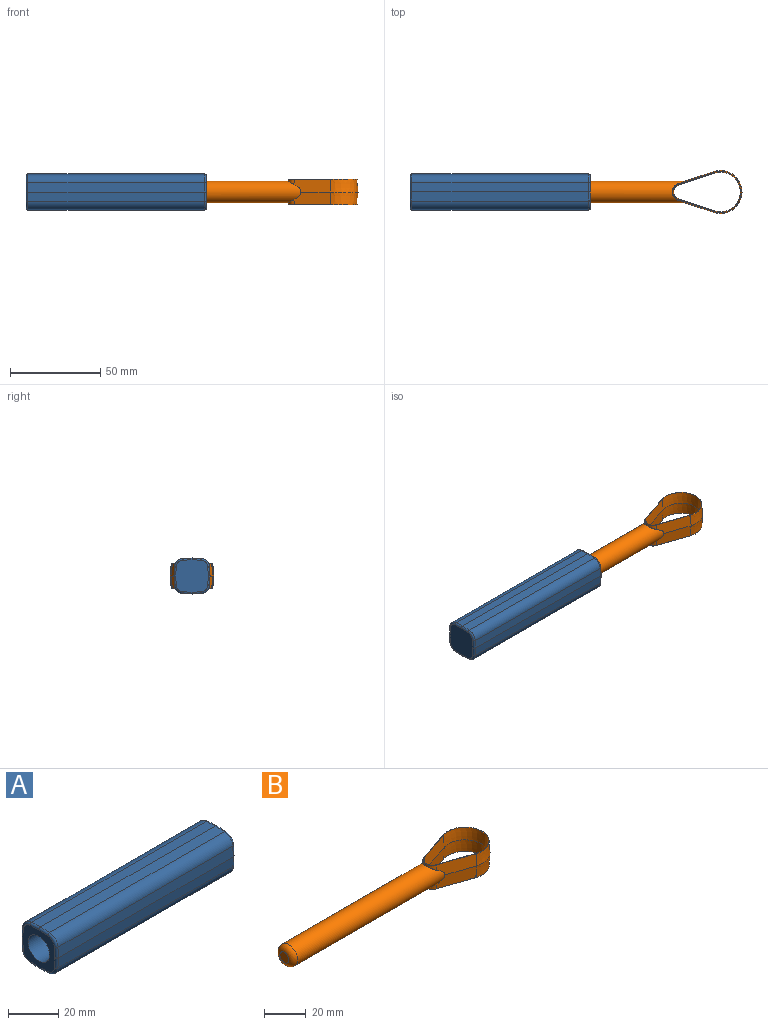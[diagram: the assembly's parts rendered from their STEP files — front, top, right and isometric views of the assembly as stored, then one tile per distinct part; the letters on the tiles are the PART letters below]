
ASSEMBLY  parts=2 mates=1
PART A: 40 faces, bbox 100x20.3x20.3 mm
  f0: plane 98x5.01mm, normal (0,1,0.05), area 491.3mm2, adj f1,f11,f22,f34
  f1: cylinder r=5mm len=98mm, axis (-1,0,0), area 718.4mm2, adj f0,f2,f20,f32
  f2: plane 98x5.01mm, normal (0,0.05,1), area 491.3mm2, adj f1,f3,f18,f30
  f3: plane 98x5.01mm, normal (0,-0.05,1), area 491.3mm2, adj f2,f4,f16,f28
  f4: cylinder r=5mm len=98mm, axis (-1,0,0), area 718.4mm2, adj f3,f5,f14,f26
  f5: plane 98x5.01mm, normal (0,-1,0.05), area 491.3mm2, adj f4,f6,f15,f27
  f6: plane 98x5.01mm, normal (0,-1,-0.05), area 491.3mm2, adj f5,f7,f17,f29
  f7: cylinder r=5mm len=98mm, axis (-1,0,0), area 718.4mm2, adj f6,f8,f19,f31
  f8: plane 98x5.01mm, normal (0,-0.05,-1), area 491.3mm2, adj f7,f9,f21,f33
  f9: plane 98x5.01mm, normal (0,0.05,-1), area 491.3mm2, adj f8,f10,f23,f35
  f10: cylinder r=5mm len=98mm, axis (-1,0,0), area 718.4mm2, adj f9,f11,f25,f37
  f11: plane 98x5.01mm, normal (0,1,-0.05), area 491.3mm2, adj f0,f10,f24,f36
  f12: plane 18x18mm, normal (1,0,0), area 297.1mm2, adj f26,f27,f28,f29,f30,f31,f32,f33
  f13: plane 18x18mm, normal (-1,0,0), area 184mm2, adj f14,f15,f16,f17,f18,f19,f20,f21
  f14: torus R=4mm, axis (1,0,0), area 10.7mm2, adj f4,f13,f15,f16
  f15: cylinder r=1mm len=5.06mm, axis (0,-0.05,-1), area 7.8mm2, adj f5,f13,f14,f17
  f16: cylinder r=1mm len=5.06mm, axis (0,-1,-0.05), area 7.8mm2, adj f3,f13,f14,f18
  f17: cylinder r=1mm len=5.06mm, axis (0,0.05,-1), area 7.8mm2, adj f6,f13,f15,f19
  f18: cylinder r=1mm len=5.06mm, axis (0,-1,0.05), area 7.8mm2, adj f2,f13,f16,f20
  f19: torus R=4mm, axis (1,0,0), area 10.7mm2, adj f7,f13,f17,f21
  f20: torus R=4mm, axis (1,0,0), area 10.7mm2, adj f1,f13,f18,f22
  f21: cylinder r=1mm len=5.06mm, axis (0,1,-0.05), area 7.8mm2, adj f8,f13,f19,f23
  f22: cylinder r=1mm len=5.06mm, axis (0,-0.05,1), area 7.8mm2, adj f0,f13,f20,f24
  f23: cylinder r=1mm len=5.06mm, axis (0,1,0.05), area 7.8mm2, adj f9,f13,f21,f25
  f24: cylinder r=1mm len=5.06mm, axis (0,0.05,1), area 7.8mm2, adj f11,f13,f22,f25
  f25: torus R=4mm, axis (1,0,0), area 10.7mm2, adj f10,f13,f23,f24
  f26: torus R=4mm, axis (1,0,0), area 10.7mm2, adj f4,f12,f27,f28
  f27: cylinder r=1mm len=5.06mm, axis (0,0.05,1), area 7.8mm2, adj f5,f12,f26,f29
  f28: cylinder r=1mm len=5.06mm, axis (0,1,0.05), area 7.8mm2, adj f3,f12,f26,f30
  f29: cylinder r=1mm len=5.06mm, axis (0,-0.05,1), area 7.8mm2, adj f6,f12,f27,f31
  f30: cylinder r=1mm len=5.06mm, axis (0,1,-0.05), area 7.8mm2, adj f2,f12,f28,f32
  f31: torus R=4mm, axis (1,0,0), area 10.7mm2, adj f7,f12,f29,f33
  f32: torus R=4mm, axis (1,0,0), area 10.7mm2, adj f1,f12,f30,f34
  f33: cylinder r=1mm len=5.06mm, axis (0,-1,0.05), area 7.8mm2, adj f8,f12,f31,f35
  f34: cylinder r=1mm len=5.06mm, axis (0,0.05,-1), area 7.8mm2, adj f0,f12,f32,f36
  f35: cylinder r=1mm len=5.06mm, axis (0,-1,-0.05), area 7.8mm2, adj f9,f12,f33,f37
  f36: cylinder r=1mm len=5.06mm, axis (0,-0.05,-1), area 7.8mm2, adj f11,f12,f34,f37
  f37: torus R=4mm, axis (1,0,0), area 10.7mm2, adj f10,f12,f35,f36
  f38: cylinder r=6mm len=50mm, axis (-1,0,0), area 1885mm2, adj f13,f39
  f39: plane 12x12mm, normal (-1,0,0), area 113.1mm2, adj f38
PART B: 21 faces, bbox 134x23.9x14 mm
  f0: plane 20.11x7.08mm, normal (-0.32,0.95,0.05), area 136.5mm2, adj f1,f3,f10,f11,f19
  f1: cone r=4.95mm half-angle=3deg, axis (0,0,-1), area 20.5mm2, adj f0,f2,f11,f19
  f2: plane 20.11x7.08mm, normal (-0.32,-0.95,0.05), area 136.5mm2, adj f1,f5,f10,f11,f19
  f3: plane 20.11x7.08mm, normal (-0.32,0.95,-0.05), area 136.5mm2, adj f0,f4,f16,f17,f19
  f4: cone r=4.95mm half-angle=3deg, axis (0,0,1), area 20.5mm2, adj f3,f5,f17,f19
  f5: plane 20.11x7.08mm, normal (-0.32,-0.95,-0.05), area 136.5mm2, adj f2,f4,f16,f17,f19
  f6: plane 19.62x7mm, normal (0.32,-0.95,0.05), area 144.2mm2, adj f7,f9,f11,f12
  f7: cone r=11mm half-angle=3deg, axis (0,0,1), area 300.8mm2, adj f6,f8,f11,f13
  f8: plane 19.62x7mm, normal (0.32,0.95,0.05), area 144.2mm2, adj f7,f9,f11,f14
  f9: cone r=4mm half-angle=3deg, axis (0,0,1), area 73.4mm2, adj f6,f8,f11,f15
  f10: cone r=11.95mm half-angle=3deg, axis (0,0,-1), area 308.6mm2, adj f0,f2,f11,f16
  f11: plane 38.17x23.17mm, normal (0,0,1), area 20.8mm2, adj f0,f1,f2,f6,f7,f8,f9,f10
  f12: plane 19.62x7mm, normal (0.32,-0.95,-0.05), area 144.2mm2, adj f6,f13,f15,f17
  f13: cone r=11mm half-angle=3deg, axis (0,0,-1), area 300.8mm2, adj f7,f12,f14,f17
  f14: plane 19.62x7mm, normal (0.32,0.95,-0.05), area 144.2mm2, adj f8,f13,f15,f17
  f15: cone r=4mm half-angle=3deg, axis (0,0,-1), area 73.4mm2, adj f9,f12,f14,f17
  f16: cone r=11.95mm half-angle=3deg, axis (0,0,1), area 308.6mm2, adj f3,f5,f10,f17
  f17: plane 38.17x23.17mm, normal (0,0,-1), area 20.8mm2, adj f3,f4,f5,f12,f13,f14,f15,f16
  f18: plane 6x6mm, normal (-1,0,0), area 28.3mm2, adj f20
  f19: cylinder r=6mm len=99.35mm, axis (-1,0,0), area 3601.7mm2, adj f0,f1,f2,f3,f4,f5,f20
  f20: torus R=3mm, axis (1,0,0), area 145.4mm2, adj f18,f19
PLACE A rot(axis=(0,0,-1),180deg) t=(-105,0,0)mm
PLACE B t=(-55,0,0)mm
MATE planar B.f19 <-> A.f38  axis (-1,0,0) through (-155,0,0)mm
